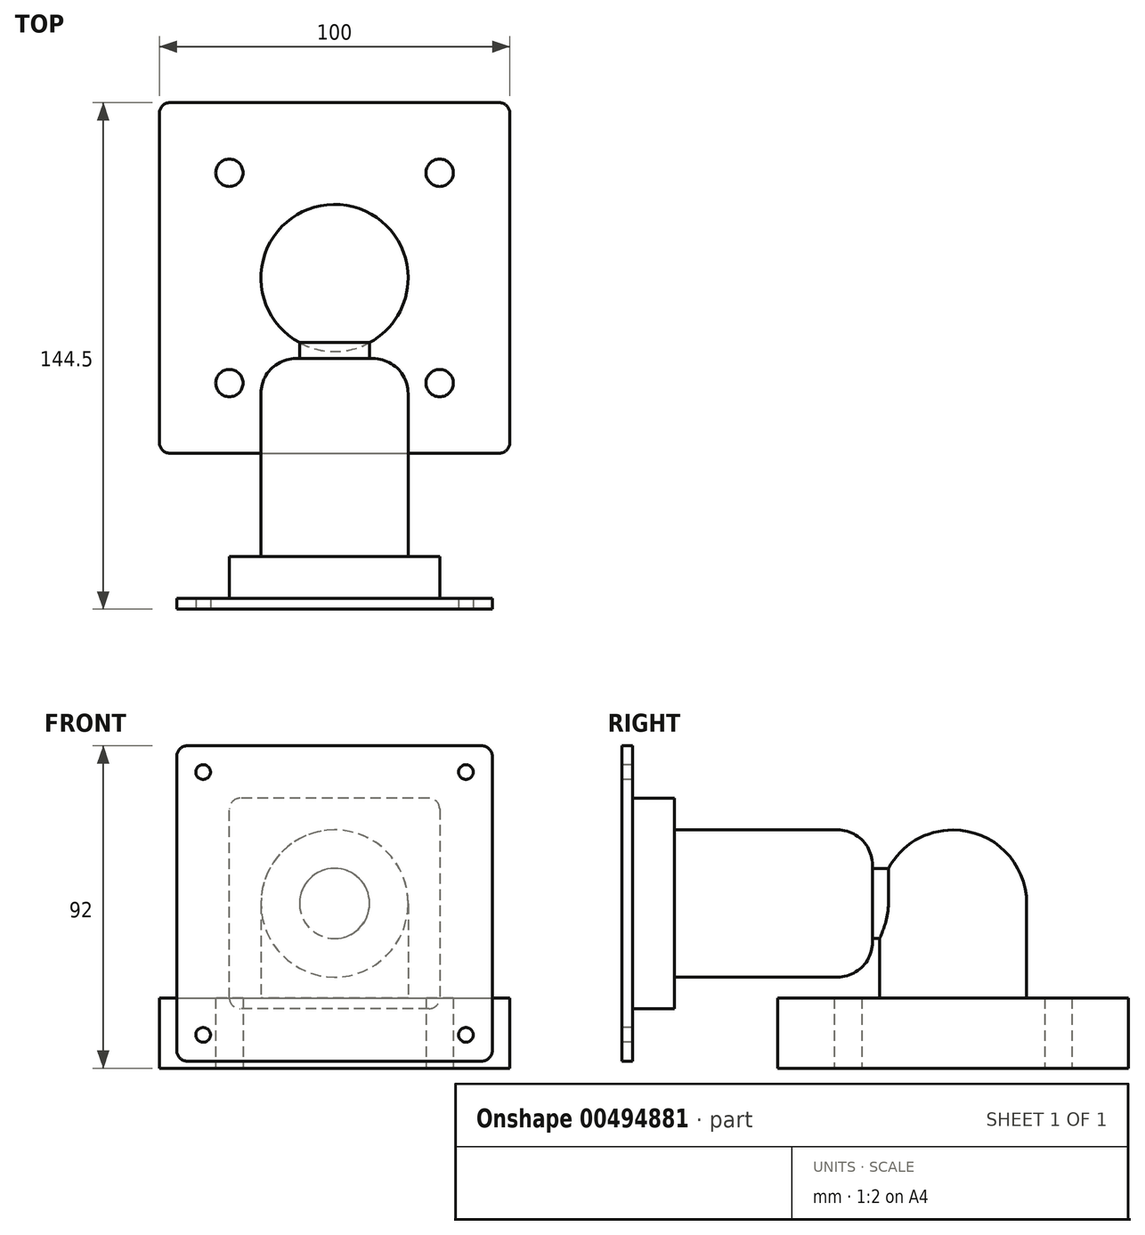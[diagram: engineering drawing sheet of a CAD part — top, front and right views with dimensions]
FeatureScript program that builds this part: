
annotation { "Feature Type Name" : "Feature", "Feature Type Description" : "" }
export const myFeature = defineFeature(function(context is Context, id is Id, definition is map)
    precondition{}
    {
        {
            var Q0;
            Q0=qCreatedBy(makeId("Top.planeOp"),FACE);
            var sketch = newSketch(context, id + "F0", { "sketchPlane" : qUnion([Q0])});
            skLineSegment(sketch, "E0.bottom", {"start": v(-50, 50) * mm, "end": v(50, 50) * mm});
            skLineSegment(sketch, "E0.top", {"start": v(-50, -50) * mm, "end": v(50, -50) * mm});
            skLineSegment(sketch, "E0.left", {"start": v(-50, 50) * mm, "end": v(-50, -50) * mm});
            skLineSegment(sketch, "E0.right", {"start": v(50, 50) * mm, "end": v(50, -50) * mm});
            skSolve(sketch);
        }
        {
            var Q0;
            Q0=qSketchRegion(id+"F0",true);
            extrude(context, id + "F1", {"entities" : qUnion([Q0]), "depth" : 20 * mm});
        }
        {
            var Q0;
            Q0=makeQuery(id+"F1.opExtrude","CAP_FACE",FACE,{"disambiguationData":[OSD([sQuery(id+"F0.wireOp",EDGE,"E0.bottom"),sQuery(id+"F0.wireOp",EDGE,"E0.top"),sQuery(id+"F0.wireOp",EDGE,"E0.left"),sQuery(id+"F0.wireOp",EDGE,"E0.right")])],"isStart":false});
            var sketch = newSketch(context, id + "F2", { "sketchPlane" : qUnion([Q0])});
            skCircle(sketch, "E1", {"center": v(0, 0) * mm, "radius": 21 * mm});
            skSolve(sketch);
        }
        {
            var Q0;
            Q0=qSketchRegion(id+"F2",true);
            extrude(context, id + "F3", {"entities" : qUnion([Q0]), "operationType" : NewBodyOperationType.ADD, "depth" : 48 * mm});
        }
        {
            var Q0;
            Q0=makeQuery(id+"F3.opExtrude","CAP_EDGE",EDGE,{"disambiguationData":[OSD([sQuery(id+"F2.wireOp",EDGE,"E1")])],"isStart":false});
            fillet(context, id + "F4", {"entities" : qUnion([Q0]), "radius" : 21 * mm, "tangentPropagation" : true, "allowEdgeOverflow" : false});
        }
        {
            var Q0;
            Q0=qCreatedBy(makeId("Front.planeOp"),FACE);
            var sketch = newSketch(context, id + "F5", { "sketchPlane" : qUnion([Q0])});
            skCircle(sketch, "E2", {"center": v(0, 47) * mm, "radius": 10 * mm});
            skSolve(sketch);
        }
        {
            var Q0;
            Q0=qSketchRegion(id+"F5",true);
            extrude(context, id + "F6", {"entities" : qUnion([Q0]), "operationType" : NewBodyOperationType.ADD, "depth" : 41 * mm});
        }
        {
            var Q0;
            Q0=makeQuery(id+"F6.opExtrude","CAP_FACE",FACE,{"disambiguationData":[OSD([sQuery(id+"F5.wireOp",EDGE,"E2")])],"isStart":false});
            var sketch = newSketch(context, id + "F7", { "sketchPlane" : qUnion([Q0])});
            skCircle(sketch, "E3", {"center": v(0, 47) * mm, "radius": 21 * mm});
            skSolve(sketch);
        }
        {
            var Q0;
            Q0=qSketchRegion(id+"F7",true);
            extrude(context, id + "F8", {"entities" : qUnion([Q0]), "operationType" : NewBodyOperationType.ADD, "depth" : 53.5 * mm, "hasSecondDirection" : true, "secondDirectionOppositeDirection" : true, "secondDirectionDepth" : 18 * mm});
        }
        {
            var Q0;
            Q0=makeQuery(id+"F8.opExtrude","CAP_EDGE",EDGE,{"disambiguationData":[OSD([sQuery(id+"F7.wireOp",EDGE,"E3")])],"isStart":true});
            fillet(context, id + "F9", {"entities" : qUnion([Q0]), "radius" : 10 * mm, "tangentPropagation" : true, "allowEdgeOverflow" : false});
        }
        {
            var Q0;
            Q0=makeQuery(id+"F8.opExtrude","CAP_FACE",FACE,{"disambiguationData":[OSD([sQuery(id+"F7.wireOp",EDGE,"E3")])],"isStart":false});
            var sketch = newSketch(context, id + "F10", { "sketchPlane" : qUnion([Q0])});
            skLineSegment(sketch, "E4.bottom", {"start": v(-30, 77) * mm, "end": v(30, 77) * mm});
            skLineSegment(sketch, "E4.top", {"start": v(-30, 17) * mm, "end": v(30, 17) * mm});
            skLineSegment(sketch, "E4.left", {"start": v(-30, 77) * mm, "end": v(-30, 17) * mm});
            skLineSegment(sketch, "E4.right", {"start": v(30, 77) * mm, "end": v(30, 17) * mm});
            skPoint(sketch, "E5", {"position": v(0, 47) * mm});
            skSolve(sketch);
        }
        {
            var Q0;
            Q0=qSketchRegion(id+"F10",true);
            extrude(context, id + "F11", {"entities" : qUnion([Q0]), "operationType" : NewBodyOperationType.ADD, "oppositeDirection" : true, "depth" : 15 * mm});
        }
        {
            var Q0;
            Q0=makeQuery(id+"F11.boolean.opBoolean","MERGE",FACE,{"derivedFrom":[makeQuery(id+"F8.opExtrude","CAP_FACE",FACE,{"disambiguationData":[OSD([sQuery(id+"F7.wireOp",EDGE,"E3")])],"isStart":false}),makeQuery(id+"F11.opExtrude","CAP_FACE",FACE,{"disambiguationData":[OSD([sQuery(id+"F10.wireOp",EDGE,"E4.bottom"),sQuery(id+"F10.wireOp",EDGE,"E4.top"),sQuery(id+"F10.wireOp",EDGE,"E4.left"),sQuery(id+"F10.wireOp",EDGE,"E4.right")])],"isStart":true})]});
            var sketch = newSketch(context, id + "F12", { "sketchPlane" : qUnion([Q0])});
            skLineSegment(sketch, "E6.bottom", {"start": v(-45, 92) * mm, "end": v(45, 92) * mm});
            skLineSegment(sketch, "E6.top", {"start": v(-45, 2) * mm, "end": v(45, 2) * mm});
            skLineSegment(sketch, "E6.left", {"start": v(-45, 92) * mm, "end": v(-45, 2) * mm});
            skLineSegment(sketch, "E6.right", {"start": v(45, 92) * mm, "end": v(45, 2) * mm});
            skSolve(sketch);
        }
        {
            var Q0;
            Q0=qSketchRegion(id+"F12",true);
            extrude(context, id + "F13", {"entities" : qUnion([Q0]), "operationType" : NewBodyOperationType.ADD, "oppositeDirection" : true, "depth" : 3 * mm});
        }
        {
            var Q0;
            Q0=makeQuery(id+"F13.boolean.opBoolean","MERGE",FACE,{"derivedFrom":[makeQuery(id+"F8.opExtrude","CAP_FACE",FACE,{"disambiguationData":[OSD([sQuery(id+"F7.wireOp",EDGE,"E3")])],"isStart":false}),makeQuery(id+"F13.opExtrude","CAP_FACE",FACE,{"disambiguationData":[OSD([sQuery(id+"F12.wireOp",EDGE,"E6.bottom"),sQuery(id+"F12.wireOp",EDGE,"E6.top"),sQuery(id+"F12.wireOp",EDGE,"E6.left"),sQuery(id+"F12.wireOp",EDGE,"E6.right")])],"isStart":true})]});
            var sketch = newSketch(context, id + "F14", { "sketchPlane" : qUnion([Q0])});
            skPoint(sketch, "E7", {"position": v(-37.5, 84.5) * mm});
            skPoint(sketch, "E8", {"position": v(37.5, 84.5) * mm});
            skPoint(sketch, "E9", {"position": v(37.5, 9.5) * mm});
            skPoint(sketch, "E10", {"position": v(-37.5, 9.5) * mm});
            skSolve(sketch);
        }
        {
            var Q0;
            Q0=sQuery(id+"F14.wireOp",VERTEX,"E7");
            var Q1;
            Q1=sQuery(id+"F14.wireOp",VERTEX,"E8");
            var Q2;
            Q2=sQuery(id+"F14.wireOp",VERTEX,"E9");
            var Q3;
            Q3=sQuery(id+"F14.wireOp",VERTEX,"E10");
            var Q4;
            Q4=makeQuery(id+"F1.opExtrude","SWEPT_BODY",BODY,{"disambiguationData":[OSD([sQuery(id+"F0.wireOp",EDGE,"E0.bottom"),sQuery(id+"F0.wireOp",EDGE,"E0.top"),sQuery(id+"F0.wireOp",EDGE,"E0.left"),sQuery(id+"F0.wireOp",EDGE,"E0.right")])]});
            hole(context, id + "F15", {"style" : HoleStyle.SIMPLE, "endStyle" : HoleEndStyle.BLIND, "standardTappedOrClearance" : lookupTablePath({ "standard" : "ISO", "size" : "4.2", "type" : "Drilled" }), "standardBlindInLast" : lookupTablePath({ "standard" : "ISO", "size" : "4.2", "type" : "Drilled" }), "holeDiameter" : 4.2 * mm, "holeDepth" : 10 * mm, "isTappedThrough" : true, "tappedDepth" : 7.6 * mm, "tapClearance" : 3, "locations" : qUnion([Q0, Q1, Q2, Q3]), "scope" : qUnion([Q4])});
        }
        {
            var Q0;
            Q0=makeQuery(id+"F1.opExtrude","CAP_FACE",FACE,{"disambiguationData":[OSD([sQuery(id+"F0.wireOp",EDGE,"E0.bottom"),sQuery(id+"F0.wireOp",EDGE,"E0.top"),sQuery(id+"F0.wireOp",EDGE,"E0.left"),sQuery(id+"F0.wireOp",EDGE,"E0.right")])],"isStart":true});
            var sketch = newSketch(context, id + "F16", { "sketchPlane" : qUnion([Q0])});
            skPoint(sketch, "E11", {"position": v(-30, 30) * mm});
            skPoint(sketch, "E12", {"position": v(30, 30) * mm});
            skPoint(sketch, "E13", {"position": v(30, -30) * mm});
            skPoint(sketch, "E14", {"position": v(-30, -30) * mm});
            skSolve(sketch);
        }
        {
            var Q0;
            Q0=sQuery(id+"F16.wireOp",VERTEX,"E11");
            var Q1;
            Q1=sQuery(id+"F16.wireOp",VERTEX,"E12");
            var Q2;
            Q2=sQuery(id+"F16.wireOp",VERTEX,"E13");
            var Q3;
            Q3=sQuery(id+"F16.wireOp",VERTEX,"E14");
            var Q4;
            Q4=makeQuery(id+"F1.opExtrude","SWEPT_BODY",BODY,{"disambiguationData":[OSD([sQuery(id+"F0.wireOp",EDGE,"E0.bottom"),sQuery(id+"F0.wireOp",EDGE,"E0.top"),sQuery(id+"F0.wireOp",EDGE,"E0.left"),sQuery(id+"F0.wireOp",EDGE,"E0.right")])]});
            hole(context, id + "F17", {"style" : HoleStyle.SIMPLE, "endStyle" : HoleEndStyle.THROUGH, "standardTappedOrClearance" : lookupTablePath({ "standard" : "ISO", "size" : "7.8", "type" : "Drilled" }), "standardBlindInLast" : lookupTablePath({ "standard" : "ISO", "size" : "7.8", "type" : "Drilled" }), "holeDiameter" : 7.8 * mm, "isTappedThrough" : true, "tappedDepth" : 7.6 * mm, "tapClearance" : 3, "locations" : qUnion([Q0, Q1, Q2, Q3]), "scope" : qUnion([Q4])});
        }
        {
            var Q0;
            Q0=makeQuery(id+"F1.opExtrude","SWEPT_EDGE",EDGE,{"disambiguationData":[OSD([sQuery(id+"F0.wireOp",EDGE,"E0.top"),sQuery(id+"F0.wireOp",EDGE,"E0.left")])]});
            var Q1;
            Q1=makeQuery(id+"F1.opExtrude","SWEPT_EDGE",EDGE,{"disambiguationData":[OSD([sQuery(id+"F0.wireOp",EDGE,"E0.bottom"),sQuery(id+"F0.wireOp",EDGE,"E0.left")])]});
            var Q2;
            Q2=makeQuery(id+"F1.opExtrude","SWEPT_EDGE",EDGE,{"disambiguationData":[OSD([sQuery(id+"F0.wireOp",EDGE,"E0.bottom"),sQuery(id+"F0.wireOp",EDGE,"E0.right")])]});
            var Q3;
            Q3=makeQuery(id+"F1.opExtrude","SWEPT_EDGE",EDGE,{"disambiguationData":[OSD([sQuery(id+"F0.wireOp",EDGE,"E0.top"),sQuery(id+"F0.wireOp",EDGE,"E0.right")])]});
            var Q4;
            Q4=makeQuery(id+"F11.opExtrude","SWEPT_EDGE",EDGE,{"disambiguationData":[OSD([sQuery(id+"F10.wireOp",EDGE,"E4.top"),sQuery(id+"F10.wireOp",EDGE,"E4.right")])]});
            var Q5;
            Q5=makeQuery(id+"F13.opExtrude","SWEPT_EDGE",EDGE,{"disambiguationData":[OSD([sQuery(id+"F12.wireOp",EDGE,"E6.top"),sQuery(id+"F12.wireOp",EDGE,"E6.right")])]});
            var Q6;
            Q6=makeQuery(id+"F11.opExtrude","SWEPT_EDGE",EDGE,{"disambiguationData":[OSD([sQuery(id+"F10.wireOp",EDGE,"E4.top"),sQuery(id+"F10.wireOp",EDGE,"E4.left")])]});
            var Q7;
            Q7=makeQuery(id+"F13.opExtrude","SWEPT_EDGE",EDGE,{"disambiguationData":[OSD([sQuery(id+"F12.wireOp",EDGE,"E6.top"),sQuery(id+"F12.wireOp",EDGE,"E6.left")])]});
            var Q8;
            Q8=makeQuery(id+"F11.opExtrude","SWEPT_EDGE",EDGE,{"disambiguationData":[OSD([sQuery(id+"F10.wireOp",EDGE,"E4.bottom"),sQuery(id+"F10.wireOp",EDGE,"E4.left")])]});
            var Q9;
            Q9=makeQuery(id+"F13.opExtrude","SWEPT_EDGE",EDGE,{"disambiguationData":[OSD([sQuery(id+"F12.wireOp",EDGE,"E6.bottom"),sQuery(id+"F12.wireOp",EDGE,"E6.left")])]});
            var Q10;
            Q10=makeQuery(id+"F11.opExtrude","SWEPT_EDGE",EDGE,{"disambiguationData":[OSD([sQuery(id+"F10.wireOp",EDGE,"E4.bottom"),sQuery(id+"F10.wireOp",EDGE,"E4.right")])]});
            var Q11;
            Q11=makeQuery(id+"F13.opExtrude","SWEPT_EDGE",EDGE,{"disambiguationData":[OSD([sQuery(id+"F12.wireOp",EDGE,"E6.bottom"),sQuery(id+"F12.wireOp",EDGE,"E6.right")])]});
            fillet(context, id + "F18", {"entities" : qUnion([Q0, Q1, Q2, Q3, Q4, Q5, Q6, Q7, Q8, Q9, Q10, Q11]), "radius" : 3 * mm, "tangentPropagation" : true, "allowEdgeOverflow" : false});
        }
    });
